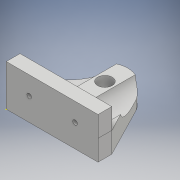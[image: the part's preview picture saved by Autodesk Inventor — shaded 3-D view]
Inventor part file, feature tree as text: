
AUTODESK INVENTOR PART (.ipt)
format: ipt  version: 2017 (Build 210142000, 142)  size: 153,088 bytes
history: native  units: mm
features: sketch x6, extrude x4
ambient origin geometry x8: Origin, YZ Plane, XZ Plane, XY Plane, X Axis, Y Axis, Z Axis, Center Point
bodies: Solid1 (feature_tree)
feature tree (10):
  sketch  "Sketch1"  dims[d9=4.5mm d10=0.0mm d11=4.5mm d12=0.0mm]
  sketch  "Sketch2"  dims[d13=1.0mm d14=1.0mm]
  sketch  "Sketch3"  dims[d15=5.5mm d16=0.0mm d17=3.0mm]
  extrude  "Extrusion1"  Depth=4.5mm TaperAngle=0.0deg
  extrude  "Extrusion2"  Depth=1.0mm
  extrude  "Extrusion3"  Depth=3.0mm
  extrude  "Extrusion4"  Depth=3.0mm
  sketch  "Sketch4"  dims[d18=3.0mm d19=11.5mm]
  sketch  "Sketch5"  dims[d23=90.0deg]
  sketch  "Sketch6"  dims[d24=90.0deg d25=10.0mm d31=5.0mm d32=120.0deg d33=14.0mm d34=6.0mm d35=6.0mm d36=10.0mm d37=0.0mm d38=5.0mm d39=5.0mm d40=5.0mm d41=5.0mm]
